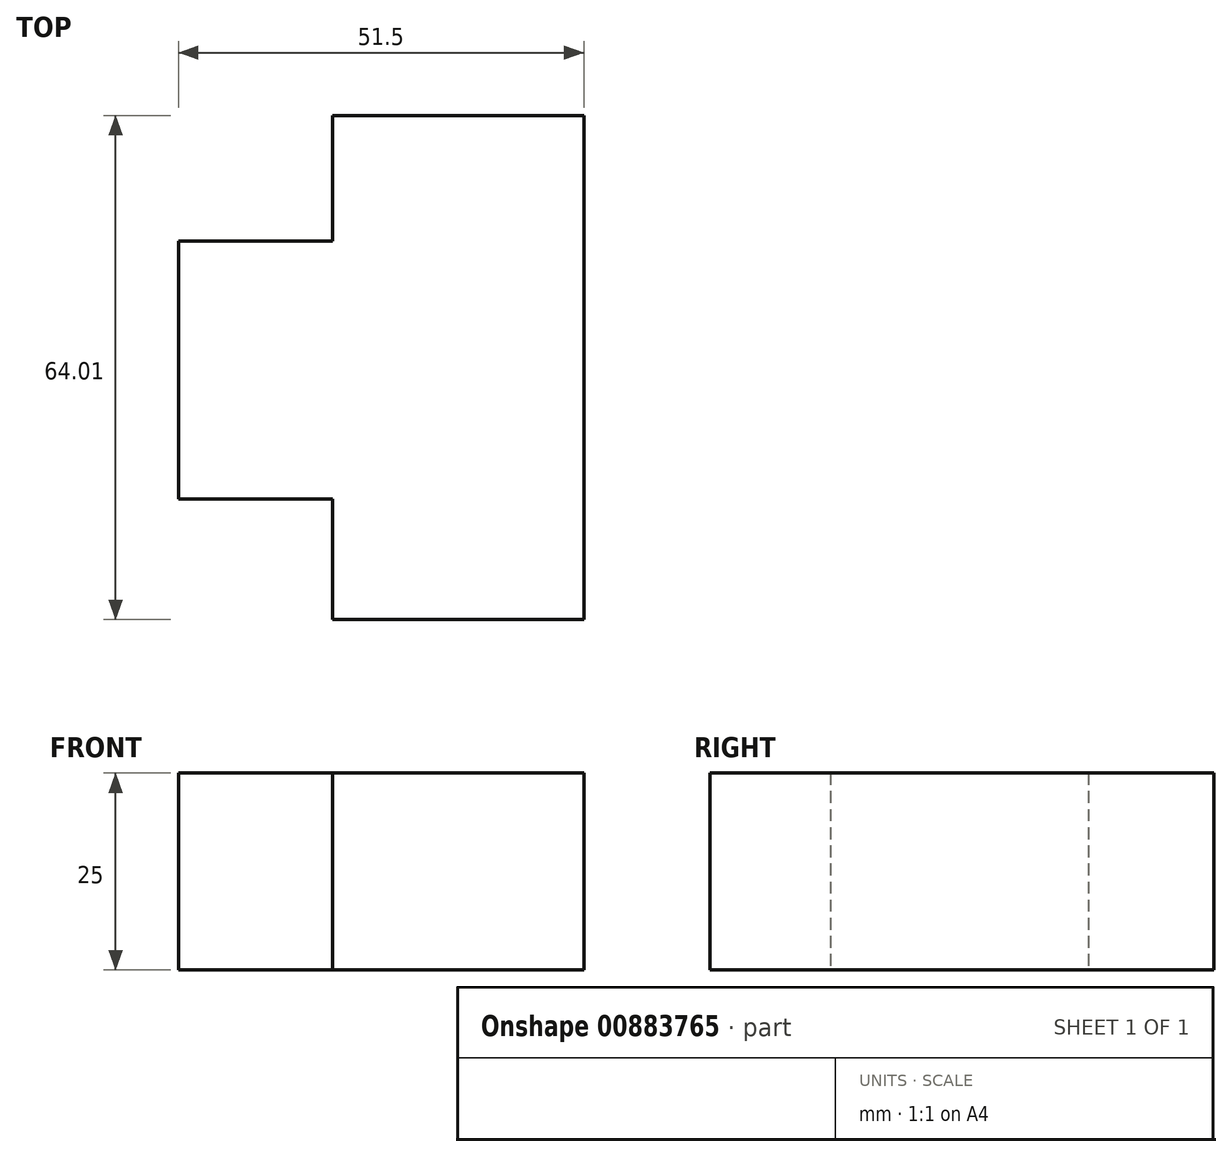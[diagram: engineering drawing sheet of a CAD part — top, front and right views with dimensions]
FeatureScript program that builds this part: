
annotation { "Feature Type Name" : "Feature", "Feature Type Description" : "" }
export const myFeature = defineFeature(function(context is Context, id is Id, definition is map)
    precondition{}
    {
        {
            var Q0;
            Q0=qCreatedBy(makeId("Top.planeOp"),FACE);
            var sketch = newSketch(context, id + "F0", { "sketchPlane" : qUnion([Q0])});
            skLineSegment(sketch, "E0.bottom", {"start": v(-31.9, 30.74) * mm, "end": v(0, 30.74) * mm});
            skLineSegment(sketch, "E0.top", {"start": v(-31.9, -33.27) * mm, "end": v(0, -33.27) * mm});
            skLineSegment(sketch, "E0.left", {"start": v(-31.9, 30.74) * mm, "end": v(-31.9, -33.27) * mm});
            skLineSegment(sketch, "E0.right", {"start": v(0, 30.74) * mm, "end": v(0, -33.27) * mm});
            skLineSegment(sketch, "E1", {"start": v(-31.9, 14.84) * mm, "end": v(-51.5, 14.84) * mm});
            skLineSegment(sketch, "E2", {"start": v(-51.5, 14.84) * mm, "end": v(-51.5, -17.94) * mm});
            skLineSegment(sketch, "E3", {"start": v(-51.5, -17.94) * mm, "end": v(-31.9, -17.94) * mm});
            skSolve(sketch);
        }
        {
            var Q0;
            Q0 = qSketchRegion(id + "F0", true);
            extrude(context, id + "F1", {"entities" : qUnion([Q0]), "depth" : 25 * mm, "offsetDistance" : 25 * mm});
        }
    });
